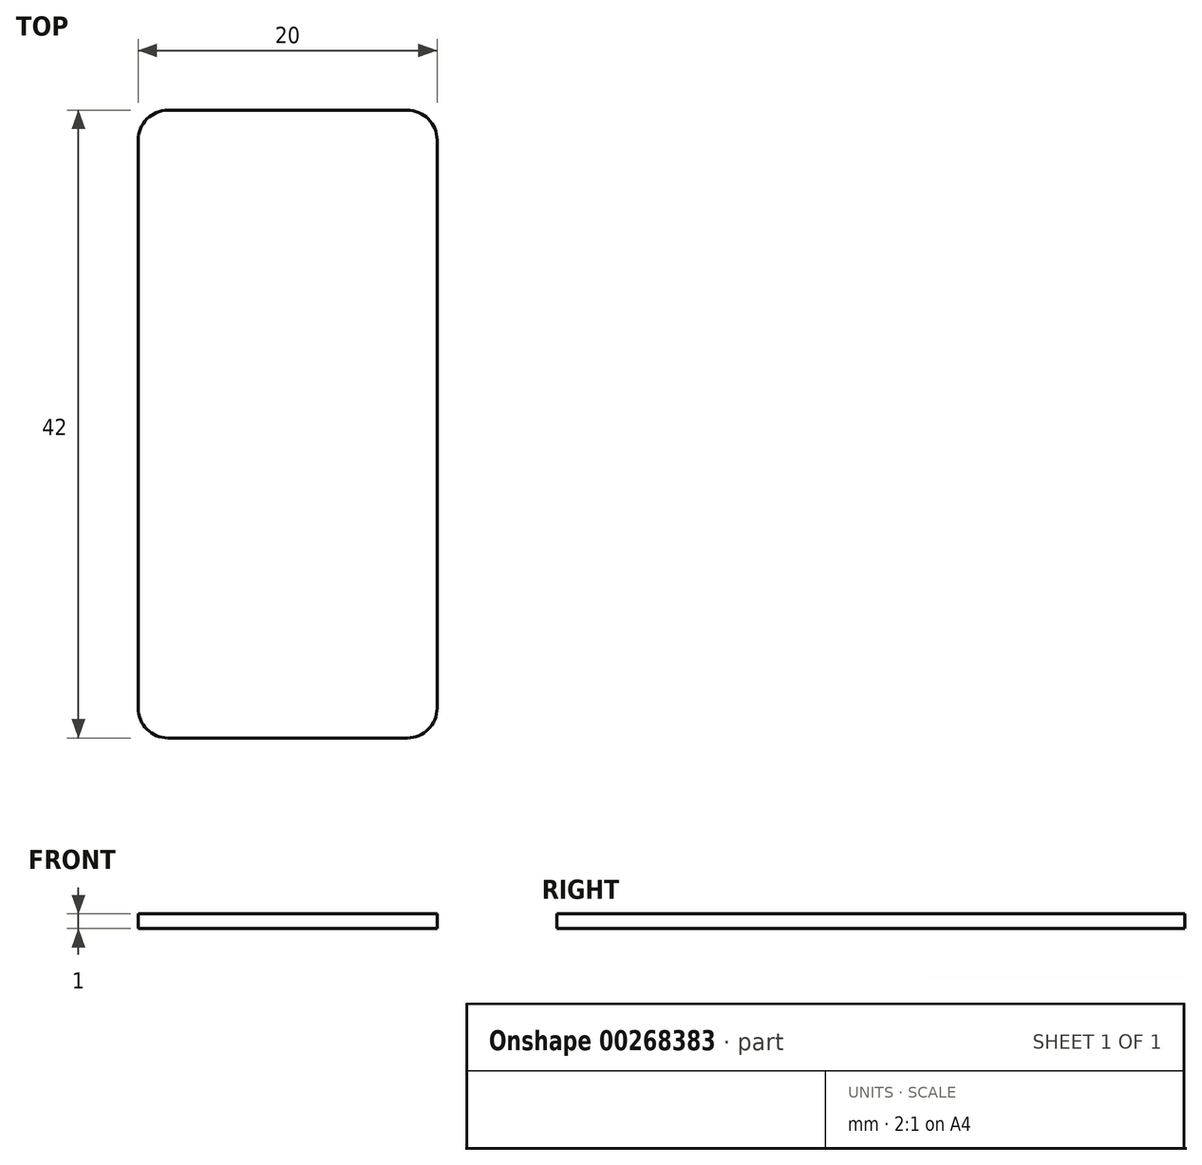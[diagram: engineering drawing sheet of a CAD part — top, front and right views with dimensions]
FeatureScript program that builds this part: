
annotation { "Feature Type Name" : "Feature", "Feature Type Description" : "" }
export const myFeature = defineFeature(function(context is Context, id is Id, definition is map)
    precondition{}
    {
        {
            var Q0;
            Q0=qCreatedBy(makeId("Top.planeOp"),FACE);
            var sketch = newSketch(context, id + "F0", { "sketchPlane" : qUnion([Q0])});
            skLineSegment(sketch, "E0.bottom", {"start": v(10, -21) * mm, "end": v(-10, -21) * mm});
            skLineSegment(sketch, "E0.top", {"start": v(10, 21) * mm, "end": v(-10, 21) * mm});
            skLineSegment(sketch, "E0.left", {"start": v(10, -21) * mm, "end": v(10, 21) * mm});
            skLineSegment(sketch, "E0.right", {"start": v(-10, -21) * mm, "end": v(-10, 21) * mm});
            skPoint(sketch, "E0.middle", {"position": v(0, 0) * mm});
            skSolve(sketch);
        }
        {
            var Q0;
            Q0=makeQuery(id+"F0.imprint","IMPRINT",FACE,{"disambiguationData":[TD([[makeQuery(id+"F0.imprint","IMPRINT",EDGE,{"derivedFrom":sQuery(id+"F0.wireOp",EDGE,"E0.bottom")}),-1.0]])]});
            extrude(context, id + "F1", {"entities" : qUnion([Q0]), "depth" : 1 * mm});
        }
        {
            var Q0;
            Q0=makeQuery(id+"F1.opExtrude","SWEPT_EDGE",EDGE,{"disambiguationData":[OSD([sQuery(id+"F0.wireOp",EDGE,"E0.bottom"),sQuery(id+"F0.wireOp",EDGE,"E0.left")])]});
            var Q1;
            Q1=makeQuery(id+"F1.opExtrude","SWEPT_EDGE",EDGE,{"disambiguationData":[OSD([sQuery(id+"F0.wireOp",EDGE,"E0.top"),sQuery(id+"F0.wireOp",EDGE,"E0.left")])]});
            var Q2;
            Q2=makeQuery(id+"F1.opExtrude","SWEPT_EDGE",EDGE,{"disambiguationData":[OSD([sQuery(id+"F0.wireOp",EDGE,"E0.top"),sQuery(id+"F0.wireOp",EDGE,"E0.right")])]});
            var Q3;
            Q3=makeQuery(id+"F1.opExtrude","SWEPT_EDGE",EDGE,{"disambiguationData":[OSD([sQuery(id+"F0.wireOp",EDGE,"E0.bottom"),sQuery(id+"F0.wireOp",EDGE,"E0.right")])]});
            fillet(context, id + "F2", {"entities" : qUnion([Q0, Q1, Q2, Q3]), "radius" : 2 * mm, "tangentPropagation" : true, "allowEdgeOverflow" : false});
        }
    });
